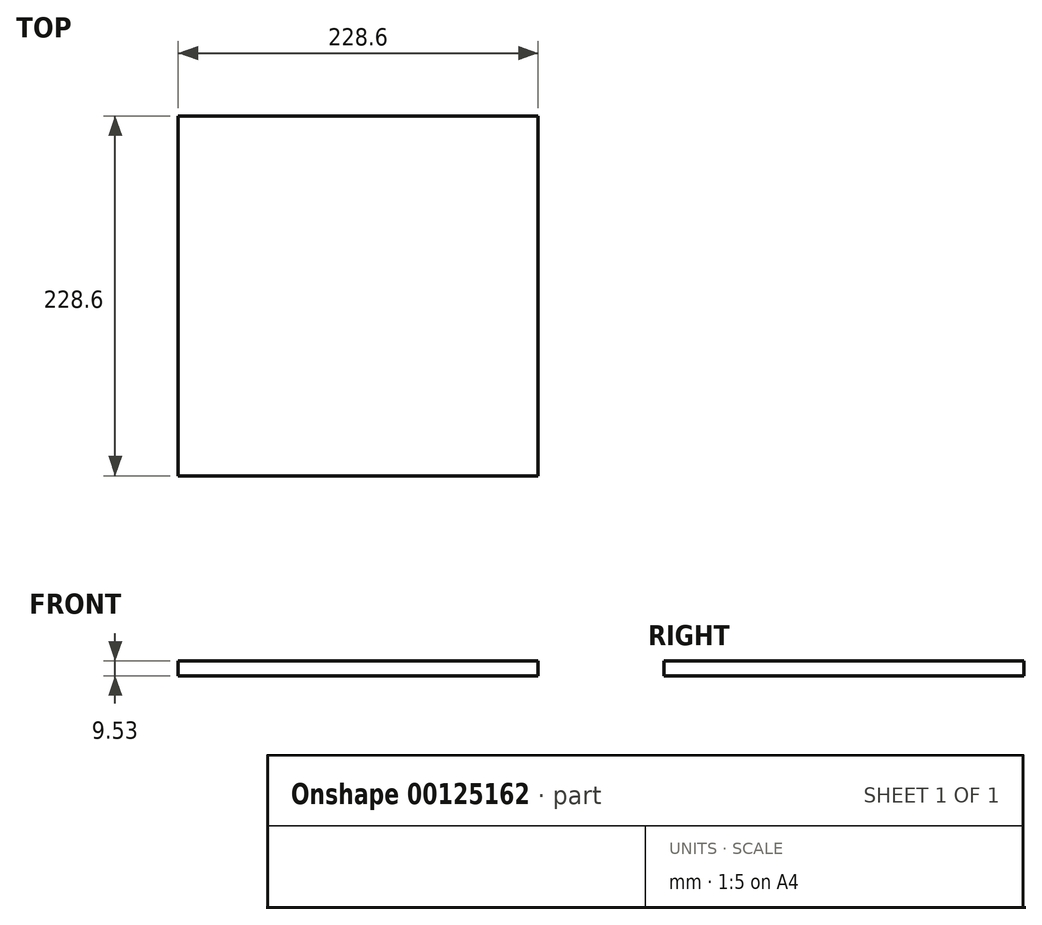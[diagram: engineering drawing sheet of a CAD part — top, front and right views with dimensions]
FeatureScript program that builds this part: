
annotation { "Feature Type Name" : "Feature", "Feature Type Description" : "" }
export const myFeature = defineFeature(function(context is Context, id is Id, definition is map)
    precondition{}
    {
        {
            var Q0;
            Q0=qCreatedBy(makeId("Top.planeOp"),FACE);
            var sketch = newSketch(context, id + "F0", { "sketchPlane" : qUnion([Q0])});
            skLineSegment(sketch, "E0.bottom", {"start": v(114.3, -114.3) * mm, "end": v(-114.3, -114.3) * mm});
            skLineSegment(sketch, "E0.top", {"start": v(114.3, 114.3) * mm, "end": v(-114.3, 114.3) * mm});
            skLineSegment(sketch, "E0.left", {"start": v(114.3, -114.3) * mm, "end": v(114.3, 114.3) * mm});
            skLineSegment(sketch, "E0.right", {"start": v(-114.3, -114.3) * mm, "end": v(-114.3, 114.3) * mm});
            skPoint(sketch, "E0.middle", {"position": v(0, 0) * mm});
            skSolve(sketch);
        }
        {
            var Q0;
            Q0=qSketchRegion(id+"F0",true);
            extrude(context, id + "F1", {"entities" : qUnion([Q0]), "oppositeDirection" : true, "depth" : 9.52 * mm});
        }
    });
